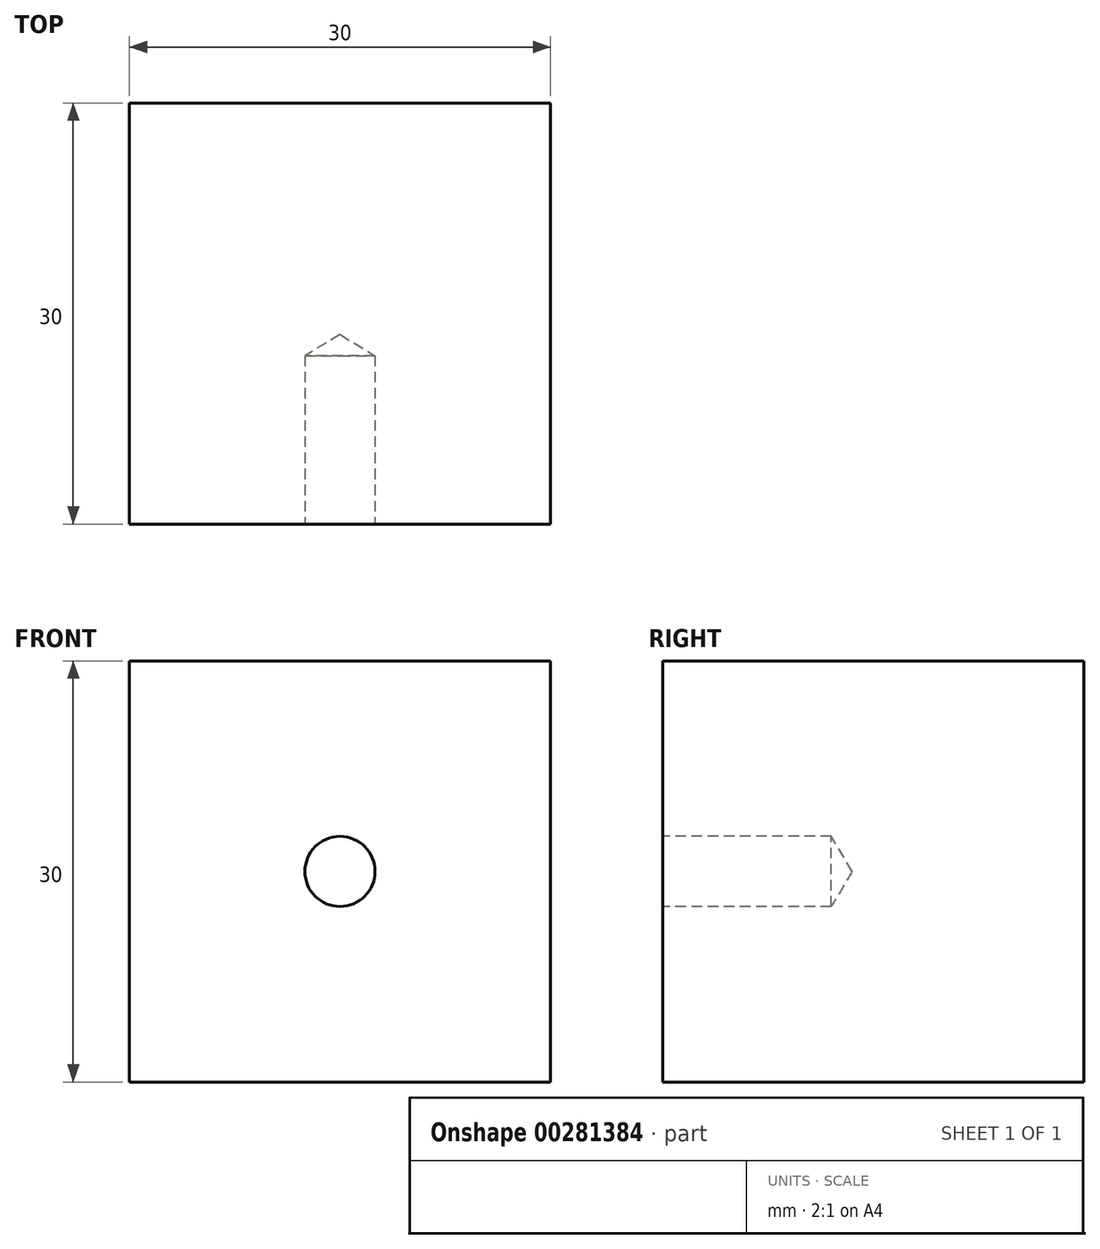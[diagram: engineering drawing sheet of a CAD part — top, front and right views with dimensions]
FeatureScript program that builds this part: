
annotation { "Feature Type Name" : "Feature", "Feature Type Description" : "" }
export const myFeature = defineFeature(function(context is Context, id is Id, definition is map)
    precondition{}
    {
        {
            var Q0;
            Q0=qCreatedBy(makeId("Front.planeOp"),FACE);
            var sketch = newSketch(context, id + "F0", { "sketchPlane" : qUnion([Q0])});
            skLineSegment(sketch, "E0.bottom", {"start": v(15, -15) * mm, "end": v(-15, -15) * mm});
            skLineSegment(sketch, "E0.top", {"start": v(15, 15) * mm, "end": v(-15, 15) * mm});
            skLineSegment(sketch, "E0.left", {"start": v(15, -15) * mm, "end": v(15, 15) * mm});
            skLineSegment(sketch, "E0.right", {"start": v(-15, -15) * mm, "end": v(-15, 15) * mm});
            skPoint(sketch, "E0.middle", {"position": v(0, 0) * mm});
            skSolve(sketch);
        }
        {
            var Q0;
            Q0=makeQuery(id+"F0.imprint","IMPRINT",FACE,{"disambiguationData":[TD([[makeQuery(id+"F0.imprint","IMPRINT",EDGE,{"derivedFrom":sQuery(id+"F0.wireOp",EDGE,"E0.bottom")}),-1.0]])]});
            extrude(context, id + "F1", {"entities" : qUnion([Q0]), "depth" : 30 * mm});
        }
        {
            var Q0;
            Q0=makeQuery(id+"F1.opExtrude","CAP_FACE",FACE,{"disambiguationData":[OSD([sQuery(id+"F0.wireOp",EDGE,"E0.bottom"),sQuery(id+"F0.wireOp",EDGE,"E0.top"),sQuery(id+"F0.wireOp",EDGE,"E0.left"),sQuery(id+"F0.wireOp",EDGE,"E0.right")])],"isStart":false});
            var sketch = newSketch(context, id + "F2", { "sketchPlane" : qUnion([Q0])});
            skPoint(sketch, "E1", {"position": v(0, 0) * mm});
            skSolve(sketch);
        }
        {
            var Q0;
            Q0=sQuery(id+"F2.wireOp",VERTEX,"E1");
            var Q1;
            Q1=makeQuery(id+"F1.opExtrude","SWEPT_BODY",BODY,{"disambiguationData":[OSD([sQuery(id+"F0.wireOp",EDGE,"E0.bottom"),sQuery(id+"F0.wireOp",EDGE,"E0.top"),sQuery(id+"F0.wireOp",EDGE,"E0.left"),sQuery(id+"F0.wireOp",EDGE,"E0.right")])]});
            hole(context, id + "F3", {"style" : HoleStyle.SIMPLE, "endStyle" : HoleEndStyle.BLIND, "holeDiameter" : 5 * mm, "holeDepth" : 12 * mm, "tappedDepth" : 12 * mm, "tapClearance" : 3, "locations" : qUnion([Q0]), "scope" : qUnion([Q1])});
        }
    });
